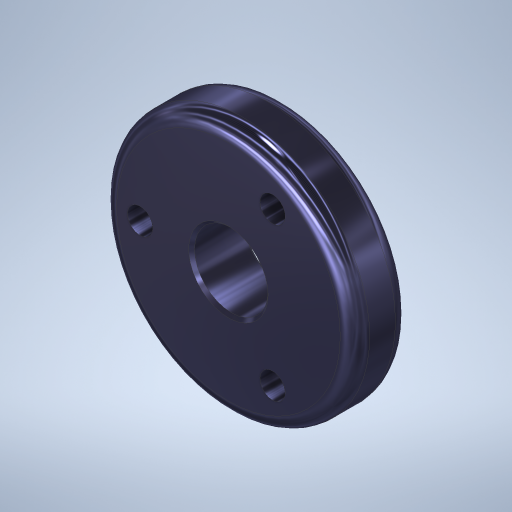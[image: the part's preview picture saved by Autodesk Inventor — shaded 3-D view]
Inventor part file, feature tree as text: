
AUTODESK INVENTOR PART (.ipt)
format: ipt  version: 2023.1 (Build 271208000, 208)  size: 327,680 bytes
history: native  units: in
note: dims shown in document units (in); Inventor stores cm internally (conversion verified against a paired STEP export)
features: extrude x2, sketch x2, fillet x1, chamfer x1, pattern_circular x1
ambient origin geometry x8: Origin, YZ Plane, XZ Plane, XY Plane, X Axis, Y Axis, Z Axis, Center Point
bodies: Solid1 (feature_tree)
feature tree (7):
  extrude  "Extrusion1"  Depth=0.0938in
  fillet  "Fillet1"  Radius=0.0938in
  chamfer  "Chamfer1"  Distance=0.005in Angle=45.0deg
  extrude  "Extrusion2"  Depth=0.025in
  pattern_circular  "Circular Pattern1"  [2 undecoded]
  sketch  "Sketch1"  dims[d0=0.125in d1=0.43in d2=0.0938in d3=0.0in]
  sketch  "Sketch2"  dims[d4=0.025in d5=0.005in d6=0.125in d7=45.0deg d8=0.043in d9=0.15in d10=0.0in d11=0.0in d12=1.1811in d13=360.0deg]
note: 2 required parameter values undecoded (feature->parameter linkage not recoverable at this tier; creation-order binding heuristic only, values carry confidence <= 0.55)
